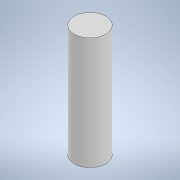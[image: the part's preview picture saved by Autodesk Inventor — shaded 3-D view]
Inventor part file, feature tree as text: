
AUTODESK INVENTOR PART (.ipt)
format: ipt  version: 2021 (Build 250183000, 183)  size: 90,112 bytes
history: native  units: in
note: dims shown in document units (in); Inventor stores cm internally (conversion verified against a paired STEP export)
features: extrude x1, sketch x1
ambient origin geometry x8: Origin, YZ Plane, XZ Plane, XY Plane, X Axis, Y Axis, Z Axis, Center Point
bodies: Solid1 (feature_tree)
feature tree (2):
  extrude  "Extrusion1"  Depth=0.625in TaperAngle=0.0deg
  sketch  "Sketch1"  dims[d0=0.175in d1=0.625in d2=0.0in]
